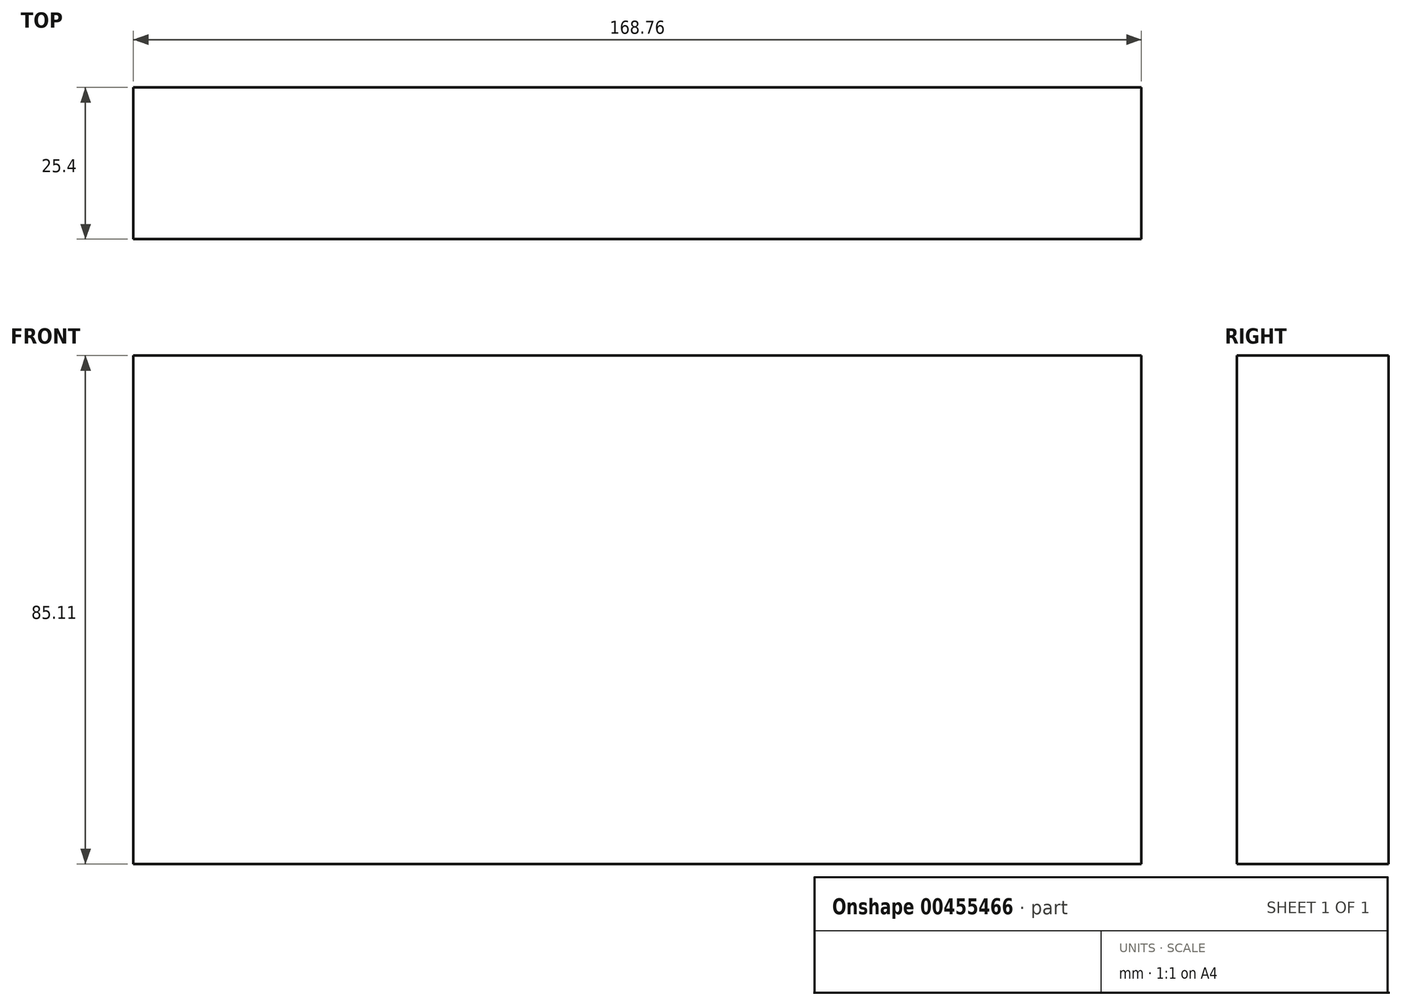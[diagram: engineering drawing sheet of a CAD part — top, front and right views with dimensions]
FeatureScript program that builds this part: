
annotation { "Feature Type Name" : "Feature", "Feature Type Description" : "" }
export const myFeature = defineFeature(function(context is Context, id is Id, definition is map)
    precondition{}
    {
        {
            var Q0;
            Q0=qCreatedBy(makeId("Front.planeOp"),FACE);
            var sketch = newSketch(context, id + "F0", { "sketchPlane" : qUnion([Q0])});
            skLineSegment(sketch, "E0.bottom", {"start": v(-59.46, 38.04) * mm, "end": v(109.3, 38.04) * mm});
            skLineSegment(sketch, "E0.top", {"start": v(-59.46, -47.07) * mm, "end": v(109.3, -47.07) * mm});
            skLineSegment(sketch, "E0.left", {"start": v(-59.46, 38.04) * mm, "end": v(-59.46, -47.07) * mm});
            skLineSegment(sketch, "E0.right", {"start": v(109.3, 38.04) * mm, "end": v(109.3, -47.07) * mm});
            skSolve(sketch);
        }
        {
            var Q0;
            Q0 = qSketchRegion(id + "F0", true);
            extrude(context, id + "F1", {"entities" : qUnion([Q0]), "depth" : 25.4 * mm});
        }
    });
